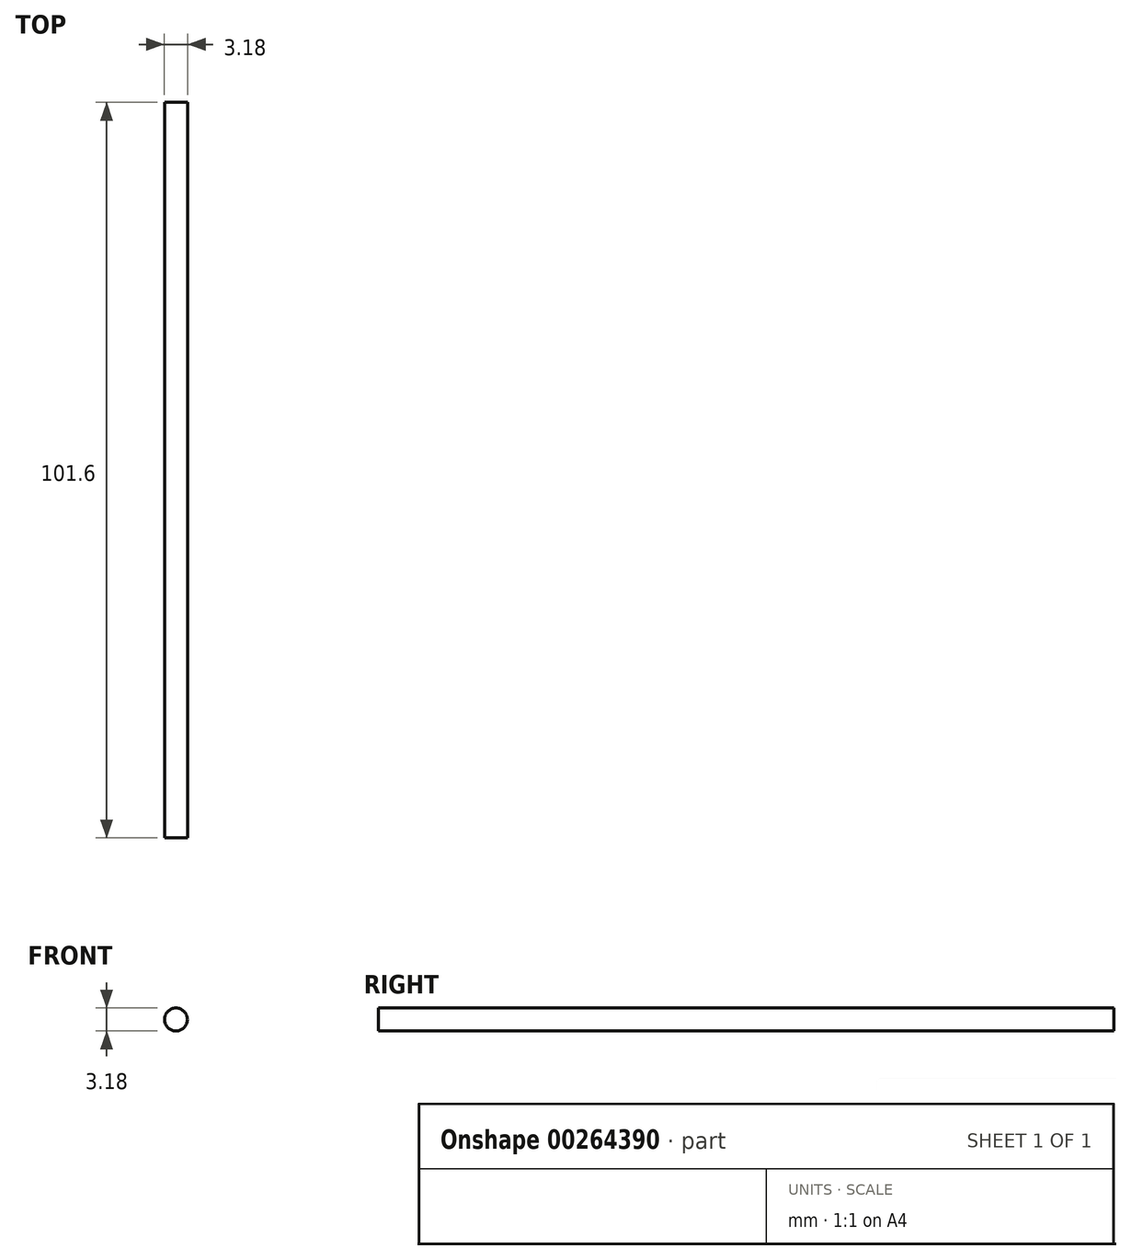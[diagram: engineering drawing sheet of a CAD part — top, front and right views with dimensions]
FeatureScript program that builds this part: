
annotation { "Feature Type Name" : "Feature", "Feature Type Description" : "" }
export const myFeature = defineFeature(function(context is Context, id is Id, definition is map)
    precondition{}
    {
        {
            var Q0;
            Q0=qCreatedBy(makeId("Front.planeOp"),FACE);
            var sketch = newSketch(context, id + "F0", { "sketchPlane" : qUnion([Q0])});
            skCircle(sketch, "E0", {"center": v(0, 0) * mm, "radius": 1.59 * mm});
            skSolve(sketch);
        }
        {
            var Q0;
            Q0=qSketchRegion(id+"F0",true);
            extrude(context, id + "F1", {"entities" : qUnion([Q0]), "depth" : 101.6 * mm});
        }
    });
